# Revit family: Access_Door-High_Security-Cendrex-All_Surface_Types-PHS
name_source: partatom
category: Specialty Equipment
revit_build: Autodesk Revit Architecture 2013 (Build: 20130531_2115(x64)
units: mm (PartAtom-declared; Revit-internal decimal feet)

## types (8) — shared parameters
Assembly Code = C1020700
Available Options = http://cendrex.com
Cendrex LEED Ready Program = http://www.cendrex.com
Construction Material = Metal - Cendrex - Aluminum
Default Elevation = 0"
Description = High security access door for all surface types
Finish = Metal - Cendrex - Powder Coated White
Frame Depth = 1 13/16"
Manufacturer = Cendrex
Model = PHS
Product Documentation Link = http://cendrex.com
Product Page URL = http://cendrex.com
URL = http://www.cendrex.com

## per-type parameters (varying)
| type | Door Height | Door Height Calc | Door Width | Door Width Calc | Height Actual | Width Actual |
| Custom | 24" | 24" | 24" | 24" | 28" | 28" |
| 12 x 12 | 12" | 12" | 12" | 12" | 16" | 16" |
| 16 x 16 | 16" | 16" | 16" | 16" | 20" | 20" |
| 18 x 18 | 18" | 18" | 18" | 18" | 22" | 22" |
| 24 x 24 | 24" | 24" | 24" | 24" | 28" | 28" |
| 24 x 30 | 30" | 30" | 24" | 24" | 34" | 28" |
| 24 x 36 | 36" | 36" | 24" | 24" | 40" | 28" |
| 36 x 36 | 36" | 36" | 36" | 36" | 40" | 40" |

## geometry (parser evidence)
native form markers: Blend x20, Sweep x8
no freeform markers — native parametric forms only
